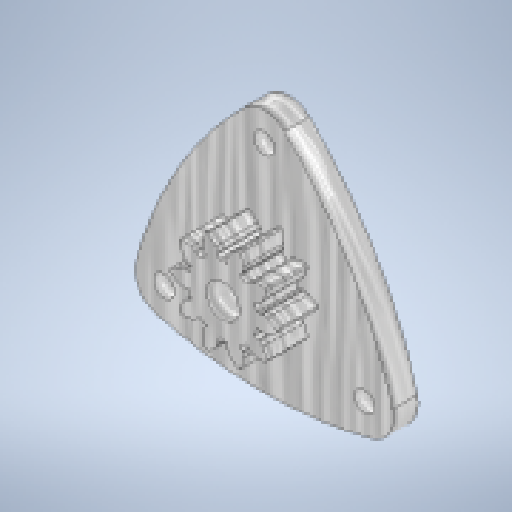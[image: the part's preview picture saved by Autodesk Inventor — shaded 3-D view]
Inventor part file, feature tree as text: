
AUTODESK INVENTOR PART (.ipt)
format: ipt  version: 2023 (Build 270158030, 158C)  size: 327,680 bytes
history: native  units: mm
features: extrude x2, sketch x2, other x1
ambient origin geometry x8: Origin, YZ Plane, XZ Plane, XY Plane, X Axis, Y Axis, Z Axis, Center Point
bodies: Body1 (feature_tree)
feature tree (5):
  other  "ソリッド1"
  extrude  "押し出し1"  Depth=30.0mm TaperAngle=360.0deg
  extrude  "押し出し2"  Depth=50.0mm
  sketch  "スケッチ1"
  sketch  "スケッチ2"
